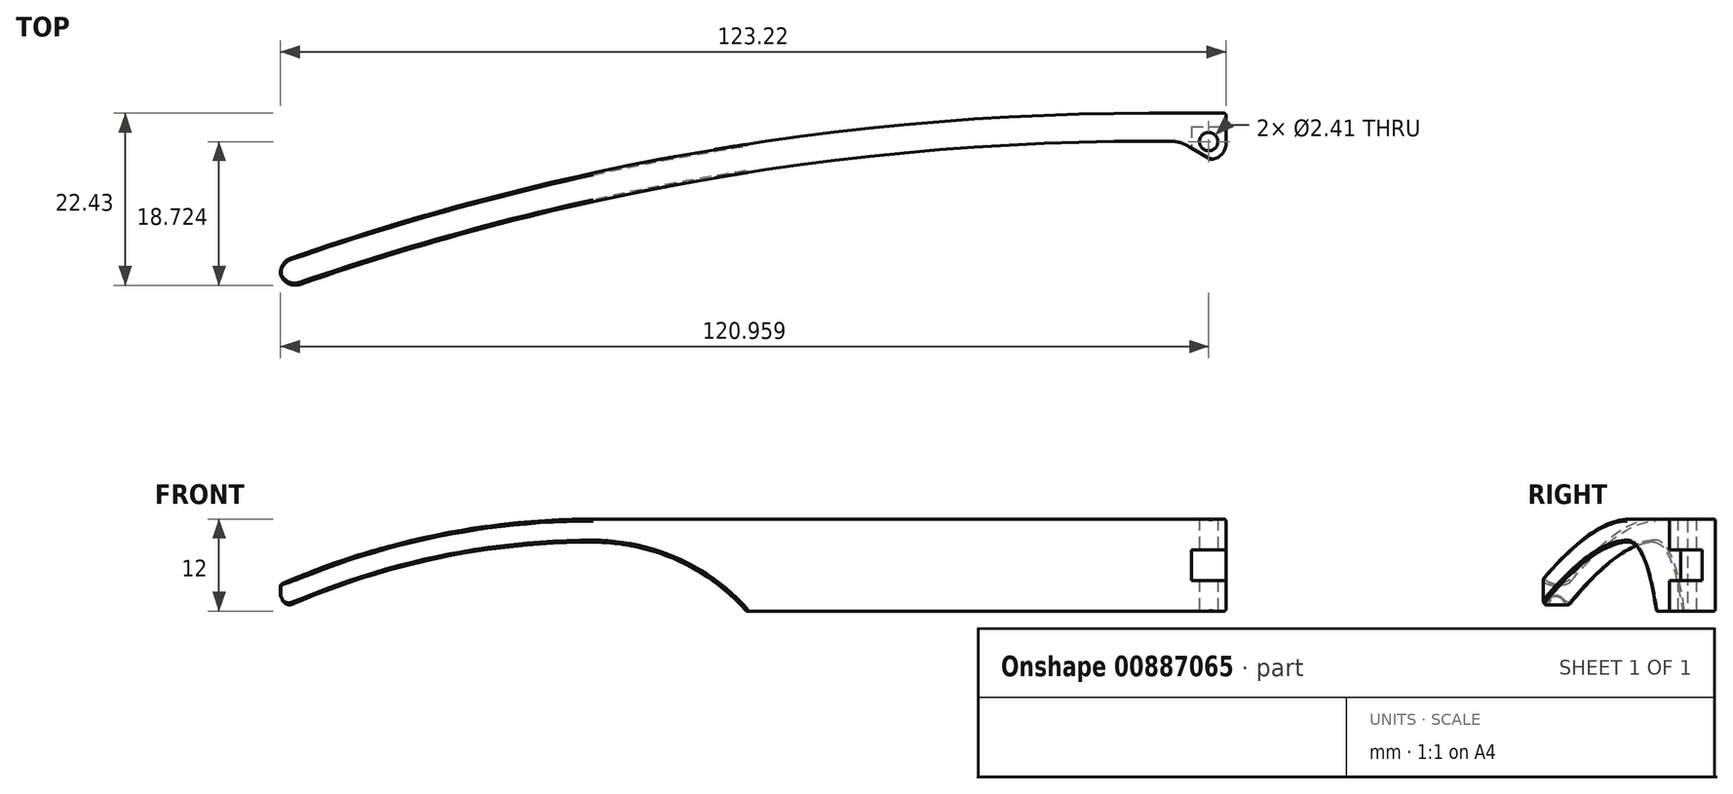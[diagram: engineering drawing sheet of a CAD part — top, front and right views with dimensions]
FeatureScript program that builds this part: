
annotation { "Feature Type Name" : "Feature", "Feature Type Description" : "" }
export const myFeature = defineFeature(function(context is Context, id is Id, definition is map)
    precondition{}
    {
        {
            var Q0;
            Q0=qCreatedBy(makeId("Top.planeOp"),FACE);
            var sketch = newSketch(context, id + "F0", { "sketchPlane" : qUnion([Q0])});
            skLineSegment(sketch, "E0", {"start": v(0, 2) * mm, "end": v(0, 6) * mm});
            skCircle(sketch, "E1", {"center": v(-2.26, 2.3) * mm, "radius": 1.2 * mm});
            skPoint(sketch, "E2.visualSharp", {"position": v(0, 0) * mm});
            skArc(sketch, "E2.filletArc", {"start": v(-1.97, 0) * mm, "mid": v(-0.58, 0.6) * mm, "end": v(0, 2) * mm});
            skLineSegment(sketch, "E3", {"start": v(-6, 2.35) * mm, "end": v(-2.02, 0.01) * mm});
            skPoint(sketch, "E4.visualSharp", {"position": v(-2, 0) * mm});
            skArc(sketch, "E4.filletArc", {"start": v(-2.02, 0.01) * mm, "mid": v(-2, 0) * mm, "end": v(-1.97, 0) * mm});
            skLineSegment(sketch, "E5", {"start": v(-10, 6) * mm, "end": v(0, 6) * mm});
            skArc(sketch, "E6", {"start": v(-10, 6) * mm, "mid": v(-67.7, 1.08) * mm, "end": v(-123.75, -13.54) * mm});
            skLineSegment(sketch, "E7", {"start": v(-6, 2.35) * mm, "end": v(-10, 2.35) * mm});
            skArc(sketch, "E8.0", {"start": v(-10, 2.35) * mm, "mid": v(-67.09, -2.52) * mm, "end": v(-122.53, -16.98) * mm});
            skLineSegment(sketch, "E9", {"start": v(-123.75, -13.54) * mm, "end": v(-122.53, -16.98) * mm});
            skSolve(sketch);
        }
        {
            var Q0;
            Q0=makeQuery(id+"F0.imprint","IMPRINT",FACE,{"disambiguationData":[TD([[makeQuery(id+"F0.imprint","IMPRINT",EDGE,{"derivedFrom":sQuery(id+"F0.wireOp",EDGE,"E0")}),1.0]])]});
            extrude(context, id + "F1", {"entities" : qUnion([Q0]), "depth" : 12 * mm, "offsetDistance" : 25 * mm});
        }
        {
            var Q0;
            Q0=makeQuery(id+"F1.opExtrude","SWEPT_EDGE",EDGE,{"disambiguationData":[OSD([sQuery(id+"F0.wireOp",EDGE,"E7"),sQuery(id+"F0.wireOp",EDGE,"E8.0")])]});
            var Q1;
            Q1=makeQuery(id+"F1.opExtrude","SWEPT_EDGE",EDGE,{"disambiguationData":[OSD([sQuery(id+"F0.wireOp",EDGE,"E8.0"),sQuery(id+"F0.wireOp",EDGE,"E9")])]});
            fillet(context, id + "F2", {"entities" : qUnion([Q0, Q1]), "radius" : 2 * mm, "tangentPropagation" : true, "allowEdgeOverflow" : false});
        }
        {
            var Q0;
            Q0=makeQuery(id+"F1.opExtrude","SWEPT_EDGE",EDGE,{"disambiguationData":[OSD([sQuery(id+"F0.wireOp",EDGE,"E6"),sQuery(id+"F0.wireOp",EDGE,"E9")])]});
            fillet(context, id + "F3", {"entities" : qUnion([Q0]), "radius" : 2 * mm, "tangentPropagation" : true, "allowEdgeOverflow" : false});
        }
        {
            var Q0;
            Q0=makeQuery(id+"F1.opExtrude","SWEPT_EDGE",EDGE,{"disambiguationData":[OSD([sQuery(id+"F0.wireOp",EDGE,"E3"),sQuery(id+"F0.wireOp",EDGE,"E7")])]});
            fillet(context, id + "F4", {"entities" : qUnion([Q0]), "radius" : 5 * mm, "tangentPropagation" : true, "allowEdgeOverflow" : false});
        }
        {
            var Q0;
            Q0=qCreatedBy(makeId("Front.planeOp"),FACE);
            var sketch = newSketch(context, id + "F5", { "sketchPlane" : qUnion([Q0])});
            skLineSegment(sketch, "E10", {"start": v(0, 0) * mm, "end": v(0, 12) * mm});
            skLineSegment(sketch, "E11", {"start": v(0, 0) * mm, "end": v(-62.5, 0) * mm});
            skPoint(sketch, "E12.visualSharp", {"position": v(-123.14, 3.27) * mm});
            skPoint(sketch, "E13.visualSharp", {"position": v(-122.3, 0.4) * mm});
            skArc(sketch, "E14", {"start": v(-62.5, 0) * mm, "mid": v(-71.53, 6.65) * mm, "end": v(-82.5, 9) * mm});
            skArc(sketch, "E15", {"start": v(-82.5, 12) * mm, "mid": v(-103.1, 9.9) * mm, "end": v(-122.86, 3.66) * mm});
            skArc(sketch, "E16.0", {"start": v(-82.5, 9) * mm, "mid": v(-102.5, 6.96) * mm, "end": v(-121.66, 0.91) * mm});
            skLineSegment(sketch, "E17", {"start": v(-123.38, 2.34) * mm, "end": v(-122.97, 1.42) * mm});
            skPoint(sketch, "E18.visualSharp", {"position": v(-123.78, 3.26) * mm});
            skArc(sketch, "E18.filletArc", {"start": v(-122.86, 3.66) * mm, "mid": v(-123.4, 3.1) * mm, "end": v(-123.38, 2.34) * mm});
            skPoint(sketch, "E19.visualSharp", {"position": v(-122.57, 0.52) * mm});
            skArc(sketch, "E19.filletArc", {"start": v(-122.97, 1.42) * mm, "mid": v(-122.42, 0.9) * mm, "end": v(-121.66, 0.91) * mm});
            skLineSegment(sketch, "E20", {"start": v(-82.5, 12) * mm, "end": v(0, 12) * mm});
            skLineSegment(sketch, "E21", {"start": v(-62.5, 0) * mm, "end": v(-123.78, 0) * mm});
            skLineSegment(sketch, "E22", {"start": v(-123.78, 0) * mm, "end": v(-123.78, 12) * mm});
            skLineSegment(sketch, "E23", {"start": v(-82.5, 12) * mm, "end": v(-84.13, 11.99) * mm});
            skLineSegment(sketch, "E24", {"start": v(-82.5, 12) * mm, "end": v(-123.78, 12) * mm});
            skSolve(sketch);
        }
        {
            var Q0;
            Q0=makeQuery(id+"F5.imprint","IMPRINT",FACE,{"disambiguationData":[TD([[makeQuery(id+"F5.imprint","IMPRINT",EDGE,{"derivedFrom":sQuery(id+"F5.wireOp",EDGE,"E14")}),1.0]])]});
            extrude(context, id + "F6", {"entities" : qUnion([Q0]), "operationType" : NewBodyOperationType.REMOVE, "endBound" : BoundingType.SYMMETRIC, "oppositeDirection" : true, "depth" : 55.2 * mm, "offsetDistance" : 25 * mm});
        }
        {
            var Q0;
            Q0=makeQuery(id+"F1.opExtrude","SWEPT_FACE",FACE,{"disambiguationData":[OSD([sQuery(id+"F0.wireOp",EDGE,"E0")])]});
            var sketch = newSketch(context, id + "F7", { "sketchPlane" : qUnion([Q0])});
            skLineSegment(sketch, "E25", {"start": v(0, 0) * mm, "end": v(6, 0) * mm});
            skLineSegment(sketch, "E26.0", {"start": v(4.25, 8) * mm, "end": v(-2.2, 8) * mm});
            skLineSegment(sketch, "E27.0", {"start": v(4.25, 4) * mm, "end": v(-2.2, 4) * mm});
            skLineSegment(sketch, "E28", {"start": v(-2.2, 8) * mm, "end": v(-2.2, 4) * mm});
            skLineSegment(sketch, "E29.0", {"start": v(4.25, 8) * mm, "end": v(4.25, 4) * mm});
            skSolve(sketch);
        }
        {
            var Q0;
            {var subQ0=sQuery(id+"F7.wireOp",EDGE,"E29.0");Q0=makeQuery(id+"F7.imprint","IMPRINT",FACE,{"disambiguationData":[TD([[makeQuery(id+"F7.imprint","IMPRINT",EDGE,{"derivedFrom":subQ0}),-1.0]])]});}
            var Q1;
            {var subQ0=sQuery(id+"F7.wireOp",EDGE,"E28");Q1=makeQuery(id+"F7.imprint","IMPRINT",FACE,{"disambiguationData":[TD([[makeQuery(id+"F7.imprint","IMPRINT",EDGE,{"derivedFrom":subQ0}),1.0]])]});}
            extrude(context, id + "F8", {"entities" : qUnion([Q0, Q1]), "operationType" : NewBodyOperationType.REMOVE, "oppositeDirection" : true, "depth" : 4.5 * mm, "offsetDistance" : 25 * mm});
        }
        {
            var Q0;
            Q0=makeQuery(id+"F1.opExtrude","CAP_EDGE",EDGE,{"disambiguationData":[OSD([sQuery(id+"F0.wireOp",EDGE,"E8.0")])],"isStart":true});
            fillet(context, id + "F9", {"entities" : qUnion([Q0]), "radius" : .25 * mm, "tangentPropagation" : true, "allowEdgeOverflow" : false});
        }
        {
            var Q0;
            Q0=makeQuery(id+"F1.opExtrude","CAP_EDGE",EDGE,{"disambiguationData":[OSD([sQuery(id+"F0.wireOp",EDGE,"E6")])],"isStart":true});
            fillet(context, id + "F10", {"entities" : qUnion([Q0]), "radius" : .25 * mm, "tangentPropagation" : true, "allowEdgeOverflow" : false});
        }
        {
            var Q0;
            Q0=makeQuery(id+"F6.boolean.opBoolean","INTERSECT",EDGE,{"derivedFrom":[makeQuery(id+"F1.opExtrude","SWEPT_FACE",FACE,{"disambiguationData":[OSD([sQuery(id+"F0.wireOp",EDGE,"E6")])]}),makeQuery(id+"F6.opExtrude","SWEPT_FACE",FACE,{"disambiguationData":[OSD([sQuery(id+"F5.wireOp",EDGE,"E16.0")])]})]});
            fillet(context, id + "F11", {"entities" : qUnion([Q0]), "radius" : .25 * mm, "tangentPropagation" : true, "allowEdgeOverflow" : false});
        }
        {
            var Q0;
            Q0=makeQuery(id+"F6.boolean.opBoolean","INTERSECT",EDGE,{"derivedFrom":[makeQuery(id+"F1.opExtrude","SWEPT_FACE",FACE,{"disambiguationData":[OSD([sQuery(id+"F0.wireOp",EDGE,"E6")])]}),makeQuery(id+"F6.opExtrude","SWEPT_FACE",FACE,{"disambiguationData":[OSD([sQuery(id+"F5.wireOp",EDGE,"E15")])]})]});
            fillet(context, id + "F12", {"entities" : qUnion([Q0]), "radius" : .25 * mm, "tangentPropagation" : true, "allowEdgeOverflow" : false});
        }
    });
